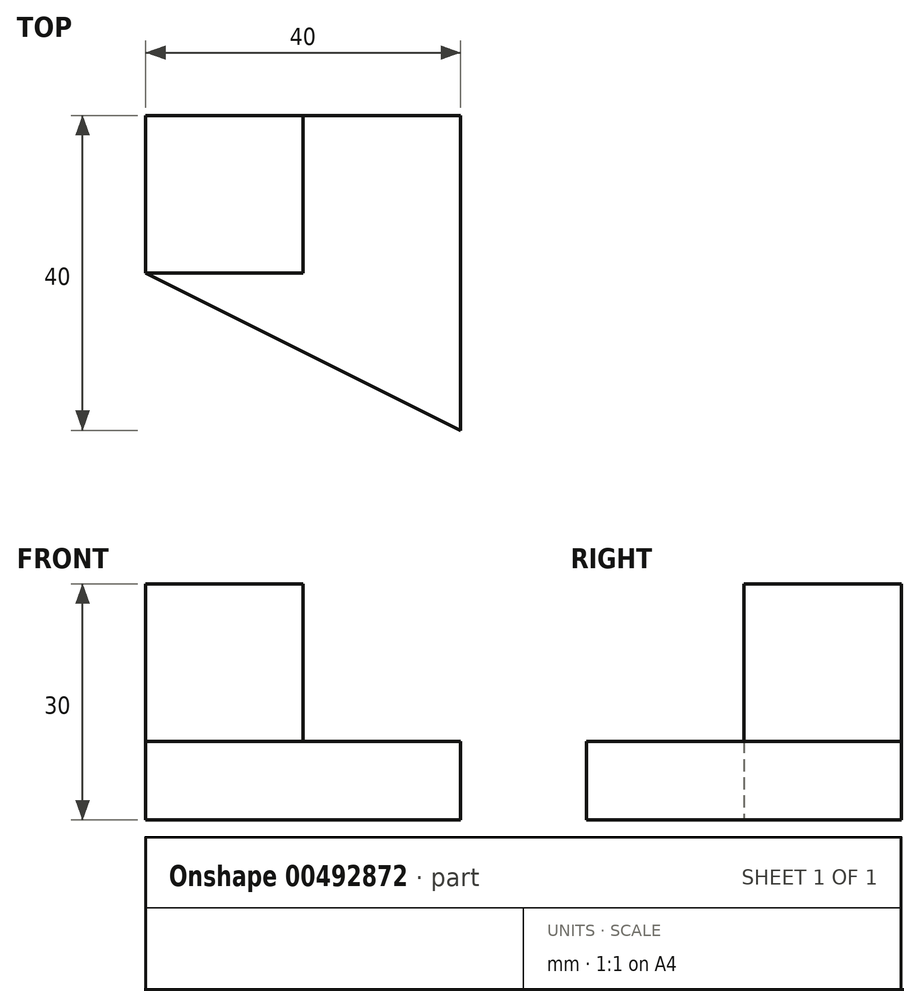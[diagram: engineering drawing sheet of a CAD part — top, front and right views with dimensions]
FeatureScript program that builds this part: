
annotation { "Feature Type Name" : "Feature", "Feature Type Description" : "" }
export const myFeature = defineFeature(function(context is Context, id is Id, definition is map)
    precondition{}
    {
        {
            var Q0;
            Q0=qCreatedBy(makeId("Top.planeOp"),FACE);
            var sketch = newSketch(context, id + "F0", { "sketchPlane" : qUnion([Q0])});
            skLineSegment(sketch, "E0", {"start": v(0, 0) * mm, "end": v(0, 20) * mm});
            skLineSegment(sketch, "E1", {"start": v(0, 20) * mm, "end": v(40, 20) * mm});
            skLineSegment(sketch, "E2", {"start": v(40, 20) * mm, "end": v(40, -20) * mm});
            skLineSegment(sketch, "E3", {"start": v(0, 0) * mm, "end": v(40, -20) * mm});
            skSolve(sketch);
        }
        {
            var Q0;
            Q0=makeQuery(id+"F0.imprint","IMPRINT",FACE,{"disambiguationData":[TD([[makeQuery(id+"F0.imprint","IMPRINT",EDGE,{"derivedFrom":sQuery(id+"F0.wireOp",EDGE,"E0")}),-1.0]])]});
            extrude(context, id + "F1", {"entities" : qUnion([Q0]), "depth" : 10 * mm});
        }
        {
            var Q0;
            Q0=makeQuery(id+"F1.opExtrude","CAP_FACE",FACE,{"disambiguationData":[OSD([sQuery(id+"F0.wireOp",EDGE,"E0"),sQuery(id+"F0.wireOp",EDGE,"E1"),sQuery(id+"F0.wireOp",EDGE,"E2"),sQuery(id+"F0.wireOp",EDGE,"E3")])],"isStart":false});
            var sketch = newSketch(context, id + "F2", { "sketchPlane" : qUnion([Q0])});
            skLineSegment(sketch, "E4", {"start": v(20, 20) * mm, "end": v(20, 0) * mm});
            skLineSegment(sketch, "E5", {"start": v(20, 0) * mm, "end": v(0, 0) * mm});
            skLineSegment(sketch, "E6", {"start": v(0, 0) * mm, "end": v(0, 20) * mm});
            skLineSegment(sketch, "E7", {"start": v(0, 20) * mm, "end": v(20, 20) * mm});
            skSolve(sketch);
        }
        {
            var Q0;
            Q0 = qSketchRegion(id + "F2", true);
            extrude(context, id + "F3", {"entities" : qUnion([Q0]), "operationType" : NewBodyOperationType.ADD, "depth" : 20 * mm});
        }
    });
